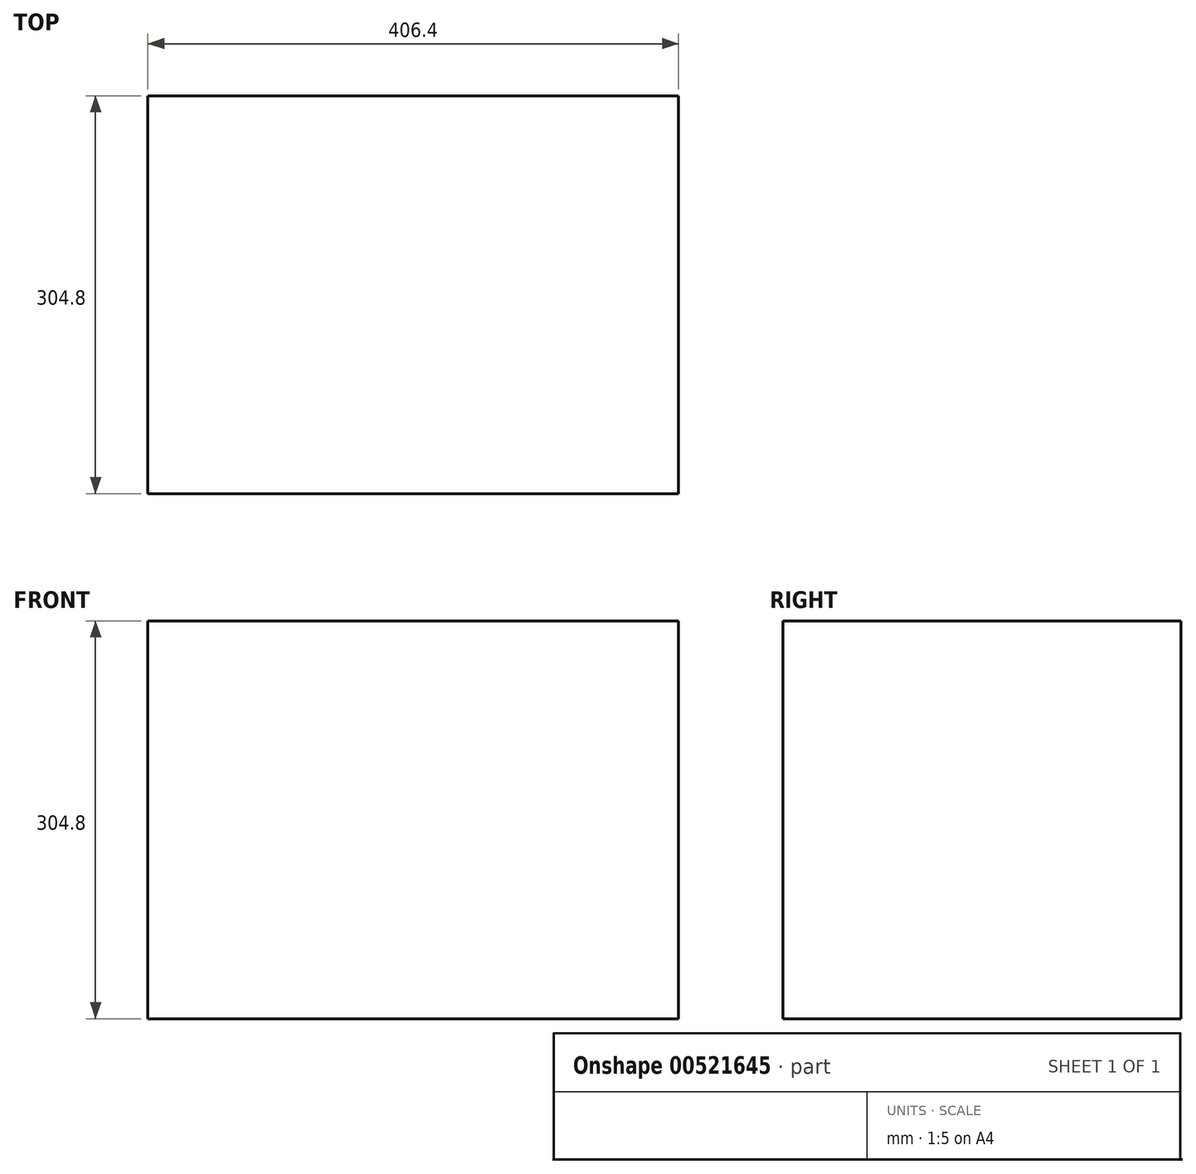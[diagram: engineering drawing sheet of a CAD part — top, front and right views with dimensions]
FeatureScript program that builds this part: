
annotation { "Feature Type Name" : "Feature", "Feature Type Description" : "" }
export const myFeature = defineFeature(function(context is Context, id is Id, definition is map)
    precondition{}
    {
        {
            var Q0;
            Q0=qCreatedBy(makeId("Top.planeOp"),FACE);
            var sketch = newSketch(context, id + "F0", { "sketchPlane" : qUnion([Q0])});
            skLineSegment(sketch, "E0.bottom", {"start": v(-203.2, 152.4) * mm, "end": v(203.2, 152.4) * mm});
            skLineSegment(sketch, "E0.top", {"start": v(-203.2, -152.4) * mm, "end": v(203.2, -152.4) * mm});
            skLineSegment(sketch, "E0.left", {"start": v(-203.2, 152.4) * mm, "end": v(-203.2, -152.4) * mm});
            skLineSegment(sketch, "E0.right", {"start": v(203.2, 152.4) * mm, "end": v(203.2, -152.4) * mm});
            skPoint(sketch, "E0.middle", {"position": v(0, 0) * mm});
            skSolve(sketch);
        }
        {
            var Q0;
            Q0 = qSketchRegion(id + "F0", true);
            extrude(context, id + "F1", {"entities" : qUnion([Q0]), "depth" : 304.8 * mm, "offsetDistance" : 25.4 * mm});
        }
    });
